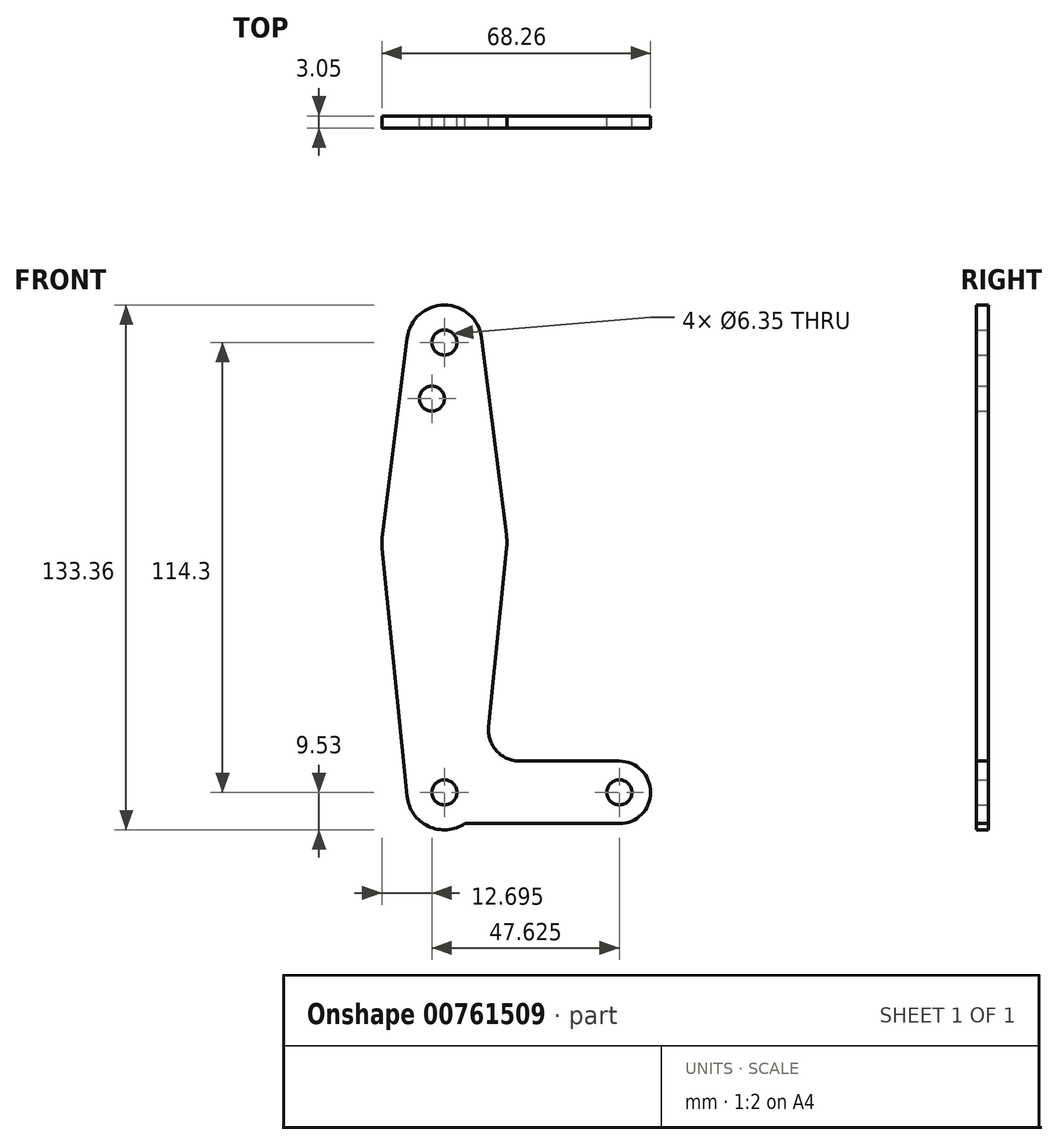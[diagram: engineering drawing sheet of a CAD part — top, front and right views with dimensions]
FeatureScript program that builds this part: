
annotation { "Feature Type Name" : "Feature", "Feature Type Description" : "" }
export const myFeature = defineFeature(function(context is Context, id is Id, definition is map)
    precondition{}
    {
        {
            var Q0;
            Q0=qCreatedBy(makeId("Front.planeOp"),FACE);
            var sketch = newSketch(context, id + "F0", { "sketchPlane" : qUnion([Q0])});
            skLineSegment(sketch, "E0", {"start": v(0, 0) * mm, "end": v(0, 114.3) * mm});
            skLineSegment(sketch, "E1", {"start": v(0, 0) * mm, "end": v(44.45, 0) * mm});
            skCircle(sketch, "E2", {"center": v(0, 114.3) * mm, "radius": 9.53 * mm});
            skCircle(sketch, "E3", {"center": v(0, 63.5) * mm, "radius": 15.88 * mm});
            skCircle(sketch, "E4", {"center": v(0, 0) * mm, "radius": 9.53 * mm});
            skCircle(sketch, "E5", {"center": v(44.45, 0) * mm, "radius": 7.94 * mm});
            skLineSegment(sketch, "E6", {"start": v(-9.45, 115.5) * mm, "end": v(-15.75, 65.48) * mm});
            skLineSegment(sketch, "E7", {"start": v(9.45, 115.5) * mm, "end": v(15.75, 65.48) * mm});
            skLineSegment(sketch, "E8", {"start": v(-15.8, 61.91) * mm, "end": v(-9.48, -0.95) * mm});
            skLineSegment(sketch, "E9", {"start": v(15.8, 61.91) * mm, "end": v(11.25, 16.68) * mm});
            skLineSegment(sketch, "E10", {"start": v(19.16, 7.94) * mm, "end": v(44.45, 7.94) * mm});
            skLineSegment(sketch, "E11", {"start": v(5.27, -7.94) * mm, "end": v(44.45, -7.94) * mm});
            skCircle(sketch, "E12", {"center": v(44.45, 0) * mm, "radius": 3.18 * mm});
            skCircle(sketch, "E13", {"center": v(0, 114.3) * mm, "radius": 3.18 * mm});
            skCircle(sketch, "E14", {"center": v(0, 0) * mm, "radius": 3.18 * mm});
            skCircle(sketch, "E15", {"center": v(-3.18, 100.03) * mm, "radius": 3.18 * mm});
            skPoint(sketch, "E16.newPointA", {"position": v(9.48, -0.95) * mm});
            skArc(sketch, "E16.filletArc", {"start": v(11.25, 16.68) * mm, "mid": v(13.26, 10.55) * mm, "end": v(19.16, 7.94) * mm});
            skSolve(sketch);
        }
        {
            var Q0;
            Q0 = qSketchRegion(id + "F0", true);
            var Q1;
            {var subQ0=sQuery(id+"F0.wireOp",EDGE,"E14");var subQ1=sQuery(id+"F0.wireOp",EDGE,"E0");var subQ2=makeQuery(id+"F0.imprint","INTERSECT",VERTEX,{"derivedFrom":[subQ1,subQ0]});Q1=makeQuery(id+"F0.imprint","IMPRINT",FACE,{"disambiguationData":[TD([[makeQuery(id+"F0.imprint","IMPRINT",EDGE,{"disambiguationData":[TD([[subQ2,-1.0]])],"derivedFrom":subQ1}),-1.0]])]});}
            extrude(context, id + "F1", {"entities" : qUnion([Q0, Q1]), "depth" : 3.05 * mm, "offsetDistance" : 25.4 * mm});
        }
    });
